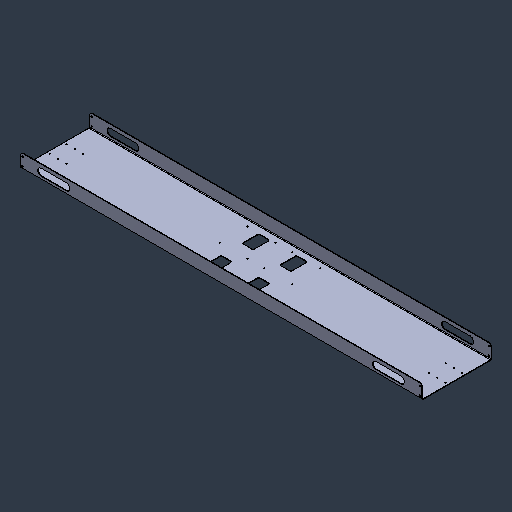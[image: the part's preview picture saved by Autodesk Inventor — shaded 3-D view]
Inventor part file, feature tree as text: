
AUTODESK INVENTOR PART (.ipt)
format: ipt  version: 2024.3 (Build 283343000, 343)  size: 163,328 bytes
history: native  units: mm (DEFAULTED — no unit token found)
features: mirror x1
ambient origin geometry x8: Origin, YZ Plane, XZ Plane, XY Plane, X Axis, Y Axis, Z Axis, Center Point
bodies: Solid1 (feature_tree)
feature tree (1):
  mirror  "Mirror2"
